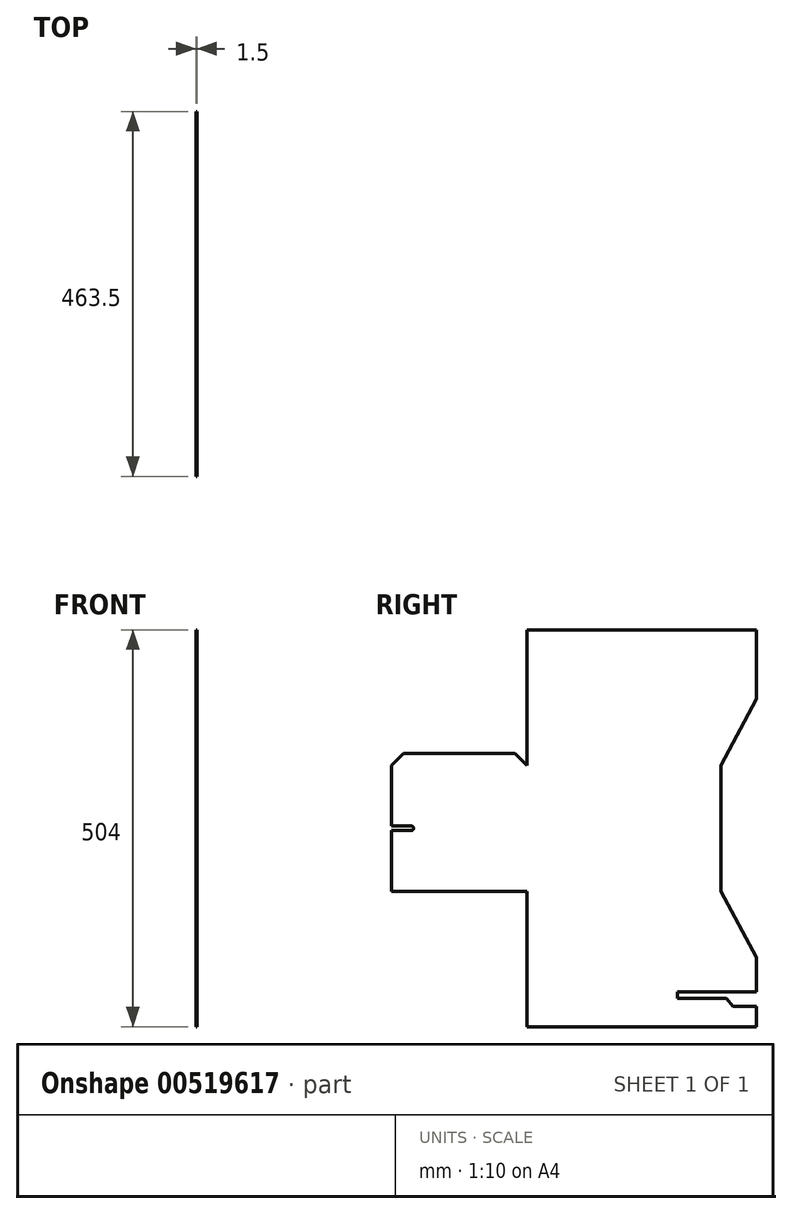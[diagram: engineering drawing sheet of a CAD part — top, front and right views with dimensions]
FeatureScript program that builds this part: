
annotation { "Feature Type Name" : "Feature", "Feature Type Description" : "" }
export const myFeature = defineFeature(function(context is Context, id is Id, definition is map)
    precondition{}
    {
        {
            var Q0;
            Q0=qCreatedBy(makeId("Right.planeOp"),FACE);
            var sketch = newSketch(context, id + "F0", { "sketchPlane" : qUnion([Q0])});
            skLineSegment(sketch, "E0.bottom", {"start": v(123.25, -80) * mm, "end": v(123.25, 80) * mm});
            skLineSegment(sketch, "E0.top", {"start": v(-123.25, -80) * mm, "end": v(-123.25, 80) * mm});
            skLineSegment(sketch, "E0.left", {"start": v(123.25, -80) * mm, "end": v(-123.25, -80) * mm});
            skLineSegment(sketch, "E0.right", {"start": v(123.25, 80) * mm, "end": v(-123.25, 80) * mm});
            skPoint(sketch, "E0.middle", {"position": v(0, 0) * mm});
            skLineSegment(sketch, "E1.top", {"start": v(168.25, -252) * mm, "end": v(-123.25, -252) * mm});
            skLineSegment(sketch, "E1.left", {"start": v(168.25, -164) * mm, "end": v(168.25, -208) * mm});
            skLineSegment(sketch, "E1.right", {"start": v(-123.25, -80) * mm, "end": v(-123.25, -252) * mm});
            skPoint(sketch, "E1.middle", {"position": v(22.5, -166) * mm});
            skLineSegment(sketch, "E2", {"start": v(123.25, -80) * mm, "end": v(168.25, -164) * mm});
            skLineSegment(sketch, "E3", {"start": v(168.25, -208) * mm, "end": v(68.25, -208) * mm});
            skLineSegment(sketch, "E4", {"start": v(68.25, -208) * mm, "end": v(68.25, -216) * mm});
            skLineSegment(sketch, "E5", {"start": v(68.25, -216) * mm, "end": v(130.25, -216) * mm});
            skLineSegment(sketch, "E6", {"start": v(130.25, -216) * mm, "end": v(138.25, -226) * mm});
            skLineSegment(sketch, "E7", {"start": v(138.25, -226) * mm, "end": v(168.25, -226) * mm});
            skLineSegment(sketch, "E8.trimOffspring", {"start": v(168.25, -226) * mm, "end": v(168.25, -252) * mm});
            skLineSegment(sketch, "E9.MirrorCS", {"start": v(168.25, 252) * mm, "end": v(-123.25, 252) * mm});
            skLineSegment(sketch, "E10.MirrorCS", {"start": v(123.25, 80) * mm, "end": v(168.25, 164) * mm});
            skLineSegment(sketch, "E11", {"start": v(168.25, 252) * mm, "end": v(168.25, 164) * mm});
            skLineSegment(sketch, "E12.top", {"start": v(-295.25, -80) * mm, "end": v(-295.25, -3) * mm});
            skLineSegment(sketch, "E12.left", {"start": v(-123.25, -80) * mm, "end": v(-295.25, -80) * mm});
            skLineSegment(sketch, "E12.right", {"start": v(-123.25, 80) * mm, "end": v(-295.25, 80) * mm});
            skPoint(sketch, "E12.middle", {"position": v(-209.25, 0) * mm});
            skArc(sketch, "E13", {"start": v(-270.25, -3) * mm, "mid": v(-267.25, 0) * mm, "end": v(-270.25, 3) * mm});
            skPoint(sketch, "E13.centerSnap0", {"position": v(-295.25, 0) * mm});
            skLineSegment(sketch, "E14.left", {"start": v(-270.25, -3) * mm, "end": v(-295.25, -3) * mm});
            skLineSegment(sketch, "E14.right", {"start": v(-270.25, 3) * mm, "end": v(-295.25, 3) * mm});
            skLineSegment(sketch, "E15.trimOffspring", {"start": v(-295.25, 3) * mm, "end": v(-295.25, 80) * mm});
            skLineSegment(sketch, "E16.bottom", {"start": v(-295.25, 80) * mm, "end": v(-123.7, 80) * mm});
            skLineSegment(sketch, "E16.top", {"start": v(-280.25, 95) * mm, "end": v(-138.25, 95) * mm});
            skLineSegment(sketch, "E17.bottom", {"start": v(-295.25, -80) * mm, "end": v(-123.25, -80) * mm});
            skLineSegment(sketch, "E17.top", {"start": v(-280.25, -95) * mm, "end": v(-138.25, -95) * mm});
            skLineSegment(sketch, "E17.right", {"start": v(-123.25, -80) * mm, "end": v(-123.25, -80) * mm});
            skLineSegment(sketch, "E18", {"start": v(-295.25, 80) * mm, "end": v(-280.25, 95) * mm});
            skLineSegment(sketch, "E19", {"start": v(-123.25, 80) * mm, "end": v(-138.25, 95) * mm});
            skLineSegment(sketch, "E20", {"start": v(-295.25, -80) * mm, "end": v(-280.25, -95) * mm});
            skLineSegment(sketch, "E21", {"start": v(-123.25, -80) * mm, "end": v(-138.25, -95) * mm});
            skLineSegment(sketch, "E22", {"start": v(-123.25, 252) * mm, "end": v(-123.25, 80) * mm});
            skSolve(sketch);
        }
        {
            var Q0;
            Q0=makeQuery(id+"F0.imprint","IMPRINT",FACE,{"disambiguationData":[TD([[makeQuery(id+"F0.imprint","IMPRINT",EDGE,{"derivedFrom":sQuery(id+"F0.wireOp",EDGE,"E0.top")}),1.0]])]});
            var Q1;
            Q1=makeQuery(id+"F0.imprint","IMPRINT",FACE,{"disambiguationData":[TD([[makeQuery(id+"F0.imprint","IMPRINT",EDGE,{"derivedFrom":sQuery(id+"F0.wireOp",EDGE,"E12.right")}),-1.0]])]});
            var Q2;
            Q2=makeQuery(id+"F0.imprint","IMPRINT",FACE,{"disambiguationData":[TD([[makeQuery(id+"F0.imprint","IMPRINT",EDGE,{"derivedFrom":sQuery(id+"F0.wireOp",EDGE,"E17.bottom")}),-1.0]])]});
            var Q3;
            Q3=makeQuery(id+"F0.imprint","IMPRINT",FACE,{"disambiguationData":[TD([[makeQuery(id+"F0.imprint","IMPRINT",EDGE,{"derivedFrom":sQuery(id+"F0.wireOp",EDGE,"E0.bottom")}),1.0]])]});
            var Q4;
            Q4=makeQuery(id+"F0.imprint","IMPRINT",FACE,{"disambiguationData":[TD([[makeQuery(id+"F0.imprint","IMPRINT",EDGE,{"derivedFrom":sQuery(id+"F0.wireOp",EDGE,"E9.MirrorCS")}),1.0]])]});
            var Q5;
            Q5=makeQuery(id+"F0.imprint","IMPRINT",FACE,{"disambiguationData":[TD([[makeQuery(id+"F0.imprint","IMPRINT",EDGE,{"derivedFrom":sQuery(id+"F0.wireOp",EDGE,"E0.left")}),1.0]])]});
            extrude(context, id + "F1", {"entities" : qUnion([Q0, Q1, Q2, Q3, Q4, Q5]), "depth" : 1.5 * mm, "offsetDistance" : 25 * mm});
        }
    });
